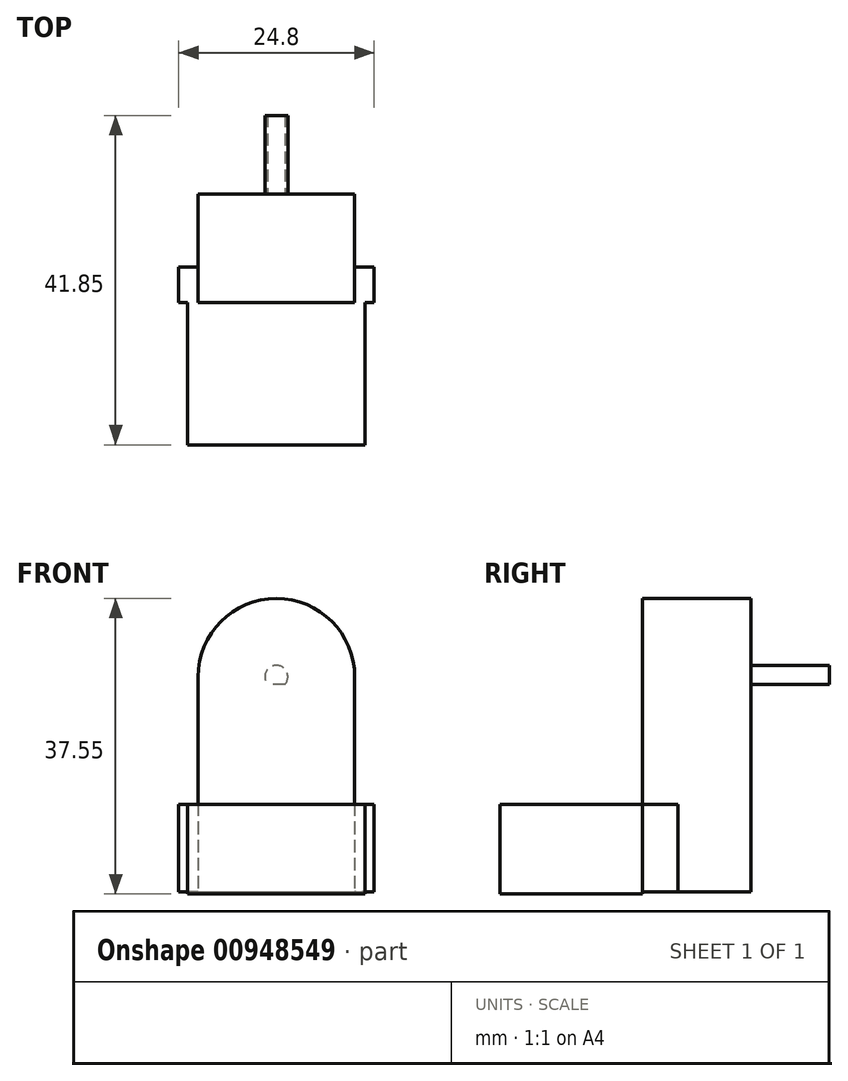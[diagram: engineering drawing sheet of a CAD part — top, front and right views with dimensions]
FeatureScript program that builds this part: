
annotation { "Feature Type Name" : "Feature", "Feature Type Description" : "" }
export const myFeature = defineFeature(function(context is Context, id is Id, definition is map)
    precondition{}
    {
        {
            var Q0;
            Q0=qCreatedBy(makeId("Front.planeOp"),FACE);
            var sketch = newSketch(context, id + "F0", { "sketchPlane" : qUnion([Q0])});
            skLineSegment(sketch, "E0.bottom", {"start": v(-9.95, 0) * mm, "end": v(9.95, 0) * mm});
            skLineSegment(sketch, "E0.top", {"start": v(-9.95, -27.35) * mm, "end": v(9.95, -27.35) * mm});
            skLineSegment(sketch, "E0.left", {"start": v(-9.95, 0) * mm, "end": v(-9.95, -27.35) * mm});
            skLineSegment(sketch, "E0.right", {"start": v(9.95, 0) * mm, "end": v(9.95, -27.35) * mm});
            skArc(sketch, "E1", {"start": v(-9.95, 0) * mm, "mid": v(0, 9.95) * mm, "end": v(9.95, 0) * mm});
            skSolve(sketch);
        }
        {
            var Q0;
            Q0 = qSketchRegion(id + "F0", true);
            extrude(context, id + "F1", {"entities" : qUnion([Q0]), "depth" : 13.75 * mm, "offsetDistance" : 25 * mm});
        }
        {
            var Q0;
            Q0=makeQuery(id+"F1.opExtrude","CAP_FACE",FACE,{"disambiguationData":[OSD([sQuery(id+"F0.wireOp",EDGE,"E0.top"),sQuery(id+"F0.wireOp",EDGE,"E0.left"),sQuery(id+"F0.wireOp",EDGE,"E0.right"),sQuery(id+"F0.wireOp",EDGE,"E1")])],"isStart":false});
            var sketch = newSketch(context, id + "F2", { "sketchPlane" : qUnion([Q0])});
            skLineSegment(sketch, "E2.bottom", {"start": v(-11.28, -27.6) * mm, "end": v(11.28, -27.6) * mm});
            skLineSegment(sketch, "E2.top", {"start": v(-11.28, -16.2) * mm, "end": v(11.27, -16.2) * mm});
            skLineSegment(sketch, "E2.left", {"start": v(-11.28, -27.6) * mm, "end": v(-11.28, -16.2) * mm});
            skLineSegment(sketch, "E2.right", {"start": v(11.27, -27.6) * mm, "end": v(11.27, -16.2) * mm});
            skPoint(sketch, "E3", {"position": v(0, -27.6) * mm});
            skSolve(sketch);
        }
        {
            var Q0;
            Q0=makeQuery(id+"F2.imprint","IMPRINT",FACE,{"disambiguationData":[TD([[makeQuery(id+"F2.imprint","IMPRINT",EDGE,{"derivedFrom":sQuery(id+"F2.wireOp",EDGE,"E2.bottom")}),1.0]])]});
            var Q1;
            {var subQ5=makeQuery(id+"F1.opExtrude","CAP_EDGE",EDGE,{"disambiguationData":[OSD([sQuery(id+"F0.wireOp",EDGE,"E0.top")])],"isStart":false});Q1=makeQuery(id+"F2.imprint","IMPRINT",FACE,{"disambiguationData":[TD([[makeQuery(id+"F2.imprint","IMPRINT",EDGE,{"derivedFrom":subQ5}),1.0]])]});}
            extrude(context, id + "F3", {"entities" : qUnion([Q0, Q1]), "operationType" : NewBodyOperationType.ADD, "depth" : 18.1 * mm, "offsetDistance" : 25 * mm});
        }
        {
            var Q0;
            Q0=makeQuery(id+"F1.opExtrude","CAP_FACE",FACE,{"disambiguationData":[OSD([sQuery(id+"F0.wireOp",EDGE,"E0.top"),sQuery(id+"F0.wireOp",EDGE,"E0.left"),sQuery(id+"F0.wireOp",EDGE,"E0.right"),sQuery(id+"F0.wireOp",EDGE,"E1")])],"isStart":false});
            var sketch = newSketch(context, id + "F4", { "sketchPlane" : qUnion([Q0])});
            skLineSegment(sketch, "E4.bottom", {"start": v(12.4, -16.2) * mm, "end": v(-12.4, -16.2) * mm});
            skLineSegment(sketch, "E4.top", {"start": v(12.4, -27.35) * mm, "end": v(-12.4, -27.35) * mm});
            skLineSegment(sketch, "E4.left", {"start": v(12.4, -16.2) * mm, "end": v(12.4, -27.35) * mm});
            skLineSegment(sketch, "E4.right", {"start": v(-12.4, -16.2) * mm, "end": v(-12.4, -27.35) * mm});
            skPoint(sketch, "E5", {"position": v(0, -27.35) * mm});
            skSolve(sketch);
        }
        {
            var Q0;
            Q0 = qSketchRegion(id + "F4", true);
            extrude(context, id + "F5", {"entities" : qUnion([Q0]), "operationType" : NewBodyOperationType.ADD, "oppositeDirection" : true, "depth" : 4.5 * mm, "offsetDistance" : 25 * mm});
        }
        {
            var Q0;
            Q0=makeQuery(id+"F1.opExtrude","CAP_FACE",FACE,{"disambiguationData":[OSD([sQuery(id+"F0.wireOp",EDGE,"E0.top"),sQuery(id+"F0.wireOp",EDGE,"E0.left"),sQuery(id+"F0.wireOp",EDGE,"E0.right"),sQuery(id+"F0.wireOp",EDGE,"E1")])],"isStart":true});
            var sketch = newSketch(context, id + "F6", { "sketchPlane" : qUnion([Q0])});
            skCircle(sketch, "E6", {"center": v(0, 0) * mm, "radius": 1.45 * mm});
            skLineSegment(sketch, "E7", {"start": v(-1.1, -0.95) * mm, "end": v(1.1, -0.95) * mm});
            skSolve(sketch);
        }
        {
            var Q0;
            {var subQ0=sQuery(id+"F6.wireOp",EDGE,"E7");Q0=makeQuery(id+"F6.imprint","IMPRINT",FACE,{"disambiguationData":[TD([[makeQuery(id+"F6.imprint","IMPRINT",EDGE,{"derivedFrom":subQ0}),1.0]])]});}
            extrude(context, id + "F7", {"entities" : qUnion([Q0]), "operationType" : NewBodyOperationType.ADD, "depth" : 10 * mm, "offsetDistance" : 25 * mm});
        }
    });
